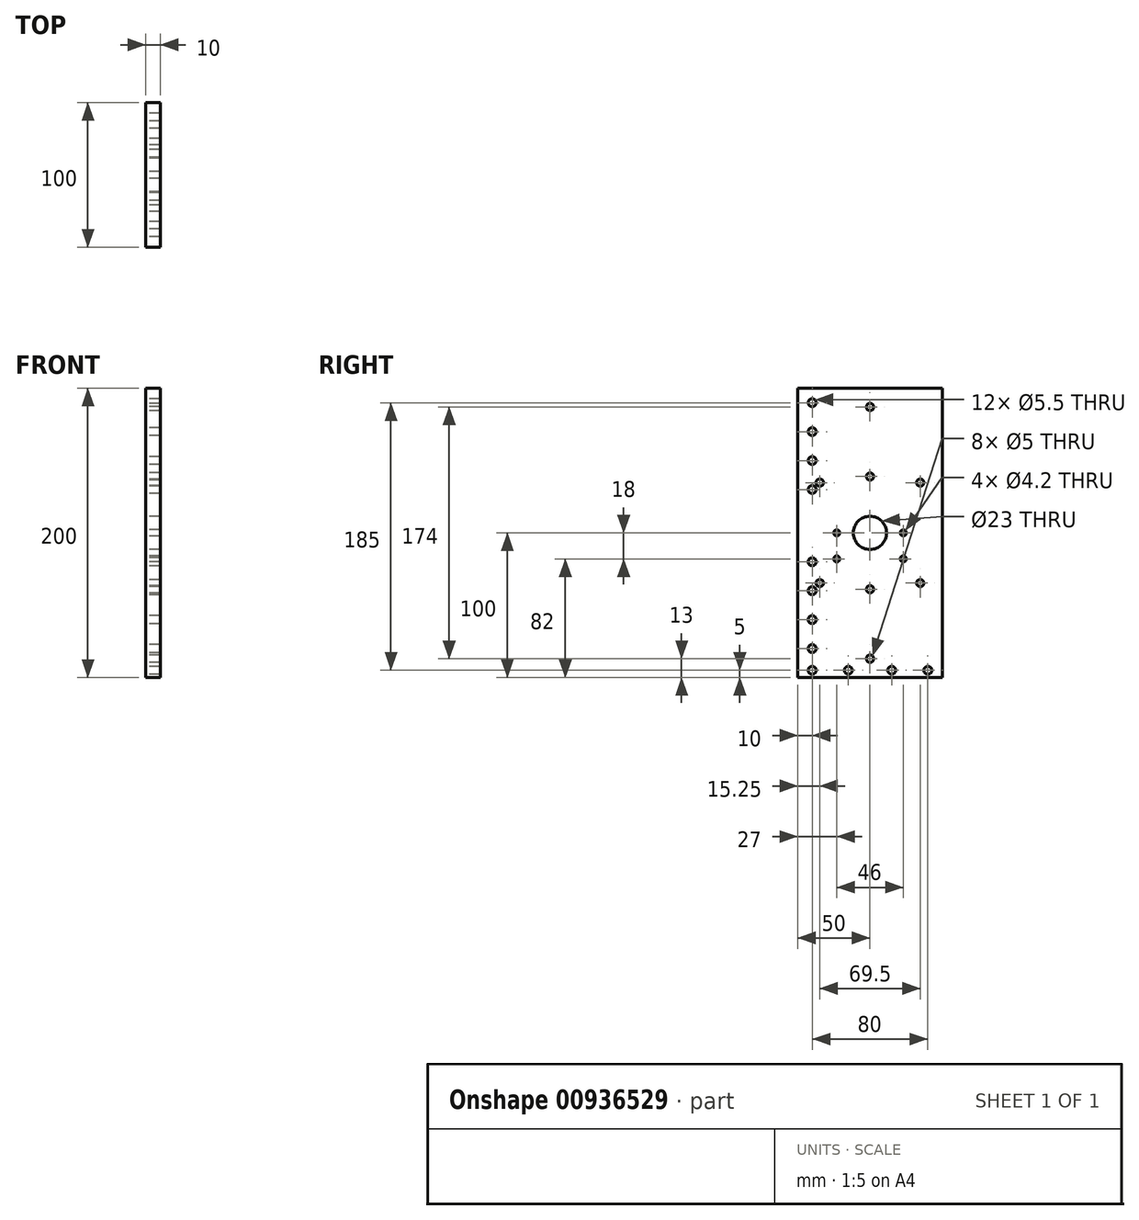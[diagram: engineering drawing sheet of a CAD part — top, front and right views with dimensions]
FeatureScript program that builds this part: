
annotation { "Feature Type Name" : "Feature", "Feature Type Description" : "" }
export const myFeature = defineFeature(function(context is Context, id is Id, definition is map)
    precondition{}
    {
        {
            var Q0;
            Q0=qCreatedBy(makeId("Right.planeOp"),FACE);
            var sketch = newSketch(context, id + "F0", { "sketchPlane" : qUnion([Q0])});
            skLineSegment(sketch, "E0.bottom", {"start": v(-50, 100) * mm, "end": v(50, 100) * mm});
            skLineSegment(sketch, "E0.top", {"start": v(-50, -100) * mm, "end": v(50, -100) * mm});
            skLineSegment(sketch, "E0.left", {"start": v(-50, 100) * mm, "end": v(-50, -100) * mm});
            skLineSegment(sketch, "E0.right", {"start": v(50, 100) * mm, "end": v(50, -100) * mm});
            skPoint(sketch, "E0.middle", {"position": v(0, 0) * mm});
            skLineSegment(sketch, "E1", {"start": v(0, 100) * mm, "end": v(0, -100) * mm, "construction": true});
            skLineSegment(sketch, "E2", {"start": v(0, 63) * mm, "end": v(26, 63) * mm, "construction": true});
            skPoint(sketch, "E3", {"position": v(0, 87) * mm});
            skPoint(sketch, "E4.MirrorP", {"position": v(0, 39) * mm});
            skLineSegment(sketch, "E5.MirrorCS", {"start": v(0, -63) * mm, "end": v(26, -63) * mm, "construction": true});
            skPoint(sketch, "E6.MirrorP", {"position": v(0, -87) * mm});
            skPoint(sketch, "E7.MirrorP", {"position": v(0, -39) * mm});
            skPoint(sketch, "E8", {"position": v(23, 0) * mm});
            skPoint(sketch, "E9.MirrorP", {"position": v(-23, 0) * mm});
            skPoint(sketch, "E10", {"position": v(23, -18) * mm});
            skPoint(sketch, "E11.MirrorP", {"position": v(-23, -18) * mm});
            skLineSegment(sketch, "E12", {"start": v(-40, 100) * mm, "end": v(-40, -100) * mm, "construction": true});
            skPoint(sketch, "E13", {"position": v(-40, 90) * mm});
            skPoint(sketch, "E14", {"position": v(-40, 70) * mm});
            skPoint(sketch, "E15", {"position": v(-40, 50) * mm});
            skPoint(sketch, "E16", {"position": v(-40, 30) * mm});
            skPoint(sketch, "E17.MirrorP", {"position": v(-40, -20) * mm});
            skPoint(sketch, "E18.MirrorP", {"position": v(-40, -40) * mm});
            skPoint(sketch, "E19.MirrorP", {"position": v(-40, -60) * mm});
            skPoint(sketch, "E20.MirrorP", {"position": v(-40, -80) * mm});
            skLineSegment(sketch, "E21", {"start": v(-50, -95) * mm, "end": v(50, -95) * mm, "construction": true});
            skPoint(sketch, "E22", {"position": v(-40, -95) * mm});
            skPoint(sketch, "E23", {"position": v(-15, -95) * mm});
            skPoint(sketch, "E24.MirrorP", {"position": v(15, -95) * mm});
            skPoint(sketch, "E25.MirrorP", {"position": v(40, -95) * mm});
            skLineSegment(sketch, "E26.bottom", {"start": v(34.75, 34.75) * mm, "end": v(-34.75, 34.75) * mm, "construction": true});
            skLineSegment(sketch, "E26.top", {"start": v(34.75, -34.75) * mm, "end": v(-34.75, -34.75) * mm, "construction": true});
            skLineSegment(sketch, "E26.left", {"start": v(34.75, 34.75) * mm, "end": v(34.75, -34.75) * mm, "construction": true});
            skLineSegment(sketch, "E26.right", {"start": v(-34.75, 34.75) * mm, "end": v(-34.75, -34.75) * mm, "construction": true});
            skPoint(sketch, "E27", {"position": v(34.75, 34.75) * mm});
            skPoint(sketch, "E28", {"position": v(-34.75, 34.75) * mm});
            skPoint(sketch, "E29", {"position": v(-34.75, -34.75) * mm});
            skPoint(sketch, "E30", {"position": v(34.75, -34.75) * mm});
            skSolve(sketch);
        }
        {
            var Q0;
            Q0=makeQuery(id+"F0.imprint","IMPRINT",FACE,{"disambiguationData":[TD([[makeQuery(id+"F0.imprint","IMPRINT",EDGE,{"derivedFrom":sQuery(id+"F0.wireOp",EDGE,"E0.bottom")}),-1.0]])]});
            extrude(context, id + "F1", {"entities" : qUnion([Q0]), "oppositeDirection" : true, "depth" : 10 * mm, "offsetDistance" : 25 * mm});
        }
        {
            var Q0;
            Q0=sQuery(id+"F0.wireOp",VERTEX,"E4.MirrorP");
            var Q1;
            Q1=sQuery(id+"F0.wireOp",VERTEX,"E3");
            var Q2;
            Q2=sQuery(id+"F0.wireOp",VERTEX,"E7.MirrorP");
            var Q3;
            Q3=sQuery(id+"F0.wireOp",VERTEX,"E6.MirrorP");
            var Q4;
            Q4=makeQuery(id+"F1.opExtrude","SWEPT_BODY",BODY,{"disambiguationData":[OSD([sQuery(id+"F0.wireOp",EDGE,"E0.bottom"),sQuery(id+"F0.wireOp",EDGE,"E0.top"),sQuery(id+"F0.wireOp",EDGE,"E0.left"),sQuery(id+"F0.wireOp",EDGE,"E0.right")])]});
            hole(context, id + "F2", {"style" : HoleStyle.SIMPLE, "endStyle" : HoleEndStyle.THROUGH, "standardTappedOrClearance" : lookupTablePath({ "standard" : "ISO", "engagement" : "75%", "pitch" : "1 mm", "size" : "M6", "type" : "Tapped" }), "standardBlindInLast" : lookupTablePath({ "standard" : "ISO", "fit" : "Normal", "engagement" : "75%", "pitch" : "1 mm", "size" : "M6", "type" : "Clearance & tapped" }), "holeDiameter" : 5 * mm, "majorDiameter" : 6 * mm, "showTappedDepth" : true, "tappedDepth" : 12 * mm, "tapClearance" : 3, "locations" : qUnion([Q0, Q1, Q2, Q3]), "scope" : qUnion([Q4]), "startStyle" : HoleStartStyle.PART});
        }
        {
            var Q0;
            Q0=sQuery(id+"F0.wireOp",VERTEX,"E11.MirrorP");
            var Q1;
            Q1=sQuery(id+"F0.wireOp",VERTEX,"E9.MirrorP");
            var Q2;
            Q2=sQuery(id+"F0.wireOp",VERTEX,"E8");
            var Q3;
            Q3=sQuery(id+"F0.wireOp",VERTEX,"E10");
            var Q4;
            Q4=makeQuery(id+"F1.opExtrude","SWEPT_BODY",BODY,{"disambiguationData":[OSD([sQuery(id+"F0.wireOp",EDGE,"E0.bottom"),sQuery(id+"F0.wireOp",EDGE,"E0.top"),sQuery(id+"F0.wireOp",EDGE,"E0.left"),sQuery(id+"F0.wireOp",EDGE,"E0.right")])]});
            hole(context, id + "F3", {"style" : HoleStyle.SIMPLE, "endStyle" : HoleEndStyle.THROUGH, "standardTappedOrClearance" : lookupTablePath({ "standard" : "ISO", "engagement" : "75%", "pitch" : "0.8 mm", "size" : "M5", "type" : "Tapped" }), "standardBlindInLast" : lookupTablePath({ "standard" : "ISO", "fit" : "Normal", "engagement" : "75%", "pitch" : "0.8 mm", "size" : "M5", "type" : "Clearance & tapped" }), "holeDiameter" : 4.2 * mm, "majorDiameter" : 5 * mm, "showTappedDepth" : true, "tappedDepth" : 12 * mm, "tapClearance" : 3, "locations" : qUnion([Q0, Q1, Q2, Q3]), "scope" : qUnion([Q4]), "startStyle" : HoleStartStyle.PART});
        }
        {
            var Q0;
            Q0=sQuery(id+"F0.wireOp",VERTEX,"E0.middle");
            var Q1;
            Q1=makeQuery(id+"F1.opExtrude","SWEPT_BODY",BODY,{"disambiguationData":[OSD([sQuery(id+"F0.wireOp",EDGE,"E0.bottom"),sQuery(id+"F0.wireOp",EDGE,"E0.top"),sQuery(id+"F0.wireOp",EDGE,"E0.left"),sQuery(id+"F0.wireOp",EDGE,"E0.right")])]});
            hole(context, id + "F4", {"style" : HoleStyle.SIMPLE, "endStyle" : HoleEndStyle.THROUGH, "standardTappedOrClearance" : lookupTablePath({ "standard" : "ISO", "size" : "23", "type" : "Drilled" }), "standardBlindInLast" : lookupTablePath({ "standard" : "ISO", "size" : "23", "type" : "Drilled" }), "holeDiameter" : 23 * mm, "majorDiameter" : 5 * mm, "tappedDepth" : 12 * mm, "tapClearance" : 3, "locations" : qUnion([Q0]), "scope" : qUnion([Q1]), "startStyle" : HoleStartStyle.PART});
        }
        {
            var Q0;
            Q0=sQuery(id+"F0.wireOp",VERTEX,"E13");
            var Q1;
            Q1=sQuery(id+"F0.wireOp",VERTEX,"E14");
            var Q2;
            Q2=sQuery(id+"F0.wireOp",VERTEX,"E15");
            var Q3;
            Q3=sQuery(id+"F0.wireOp",VERTEX,"E16");
            var Q4;
            Q4=sQuery(id+"F0.wireOp",VERTEX,"E17.MirrorP");
            var Q5;
            Q5=sQuery(id+"F0.wireOp",VERTEX,"E18.MirrorP");
            var Q6;
            Q6=sQuery(id+"F0.wireOp",VERTEX,"E19.MirrorP");
            var Q7;
            Q7=sQuery(id+"F0.wireOp",VERTEX,"E20.MirrorP");
            var Q8;
            Q8=makeQuery(id+"F1.opExtrude","SWEPT_BODY",BODY,{"disambiguationData":[OSD([sQuery(id+"F0.wireOp",EDGE,"E0.bottom"),sQuery(id+"F0.wireOp",EDGE,"E0.top"),sQuery(id+"F0.wireOp",EDGE,"E0.left"),sQuery(id+"F0.wireOp",EDGE,"E0.right")])]});
            hole(context, id + "F5", {"style" : HoleStyle.SIMPLE, "endStyle" : HoleEndStyle.THROUGH, "standardTappedOrClearance" : lookupTablePath({ "fit" : "Normal", "standard" : "ISO", "size" : "M5", "type" : "Clearance" }), "standardBlindInLast" : lookupTablePath({ "fit" : "Normal", "standard" : "ISO", "engagement" : "75%", "pitch" : "0.8 mm", "size" : "M5", "type" : "Clearance & tapped" }), "holeDiameter" : 5.5 * mm, "majorDiameter" : 5 * mm, "tappedDepth" : 12 * mm, "tapClearance" : 3, "locations" : qUnion([Q0, Q1, Q2, Q3, Q4, Q5, Q6, Q7]), "scope" : qUnion([Q8]), "startStyle" : HoleStartStyle.PART});
        }
        {
            var Q0;
            Q0=sQuery(id+"F0.wireOp",VERTEX,"E22");
            var Q1;
            Q1=sQuery(id+"F0.wireOp",VERTEX,"E23");
            var Q2;
            Q2=sQuery(id+"F0.wireOp",VERTEX,"E24.MirrorP");
            var Q3;
            Q3=sQuery(id+"F0.wireOp",VERTEX,"E25.MirrorP");
            var Q4;
            Q4=makeQuery(id+"F1.opExtrude","SWEPT_BODY",BODY,{"disambiguationData":[OSD([sQuery(id+"F0.wireOp",EDGE,"E0.bottom"),sQuery(id+"F0.wireOp",EDGE,"E0.top"),sQuery(id+"F0.wireOp",EDGE,"E0.left"),sQuery(id+"F0.wireOp",EDGE,"E0.right")])]});
            hole(context, id + "F6", {"style" : HoleStyle.SIMPLE, "endStyle" : HoleEndStyle.THROUGH, "standardTappedOrClearance" : lookupTablePath({ "fit" : "Normal", "standard" : "ISO", "size" : "M5", "type" : "Clearance" }), "standardBlindInLast" : lookupTablePath({ "fit" : "Normal", "standard" : "ISO", "engagement" : "75%", "pitch" : "0.8 mm", "size" : "M5", "type" : "Clearance & tapped" }), "holeDiameter" : 5.5 * mm, "majorDiameter" : 5 * mm, "tappedDepth" : 12 * mm, "tapClearance" : 3, "locations" : qUnion([Q0, Q1, Q2, Q3]), "scope" : qUnion([Q4]), "startStyle" : HoleStartStyle.PART});
        }
        {
            var Q0;
            Q0=sQuery(id+"F0.wireOp",VERTEX,"E27");
            var Q1;
            Q1=sQuery(id+"F0.wireOp",VERTEX,"E28");
            var Q2;
            Q2=sQuery(id+"F0.wireOp",VERTEX,"E29");
            var Q3;
            Q3=sQuery(id+"F0.wireOp",VERTEX,"E30");
            var Q4;
            Q4=makeQuery(id+"F1.opExtrude","SWEPT_BODY",BODY,{"disambiguationData":[OSD([sQuery(id+"F0.wireOp",EDGE,"E0.bottom"),sQuery(id+"F0.wireOp",EDGE,"E0.top"),sQuery(id+"F0.wireOp",EDGE,"E0.left"),sQuery(id+"F0.wireOp",EDGE,"E0.right")])]});
            hole(context, id + "F7", {"style" : HoleStyle.SIMPLE, "endStyle" : HoleEndStyle.BLIND, "standardTappedOrClearance" : lookupTablePath({ "standard" : "ISO", "engagement" : "75%", "pitch" : "1 mm", "size" : "M6", "type" : "Tapped" }), "standardBlindInLast" : lookupTablePath({ "standard" : "ISO", "fit" : "Normal", "engagement" : "75%", "pitch" : "1 mm", "size" : "M6", "type" : "Clearance & tapped" }), "holeDiameter" : 5 * mm, "majorDiameter" : 6 * mm, "showTappedDepth" : true, "holeDepth" : 15 * mm, "tappedDepth" : 12 * mm, "tapClearance" : 3, "locations" : qUnion([Q0, Q1, Q2, Q3]), "scope" : qUnion([Q4]), "startStyle" : HoleStartStyle.PART});
        }
    });
